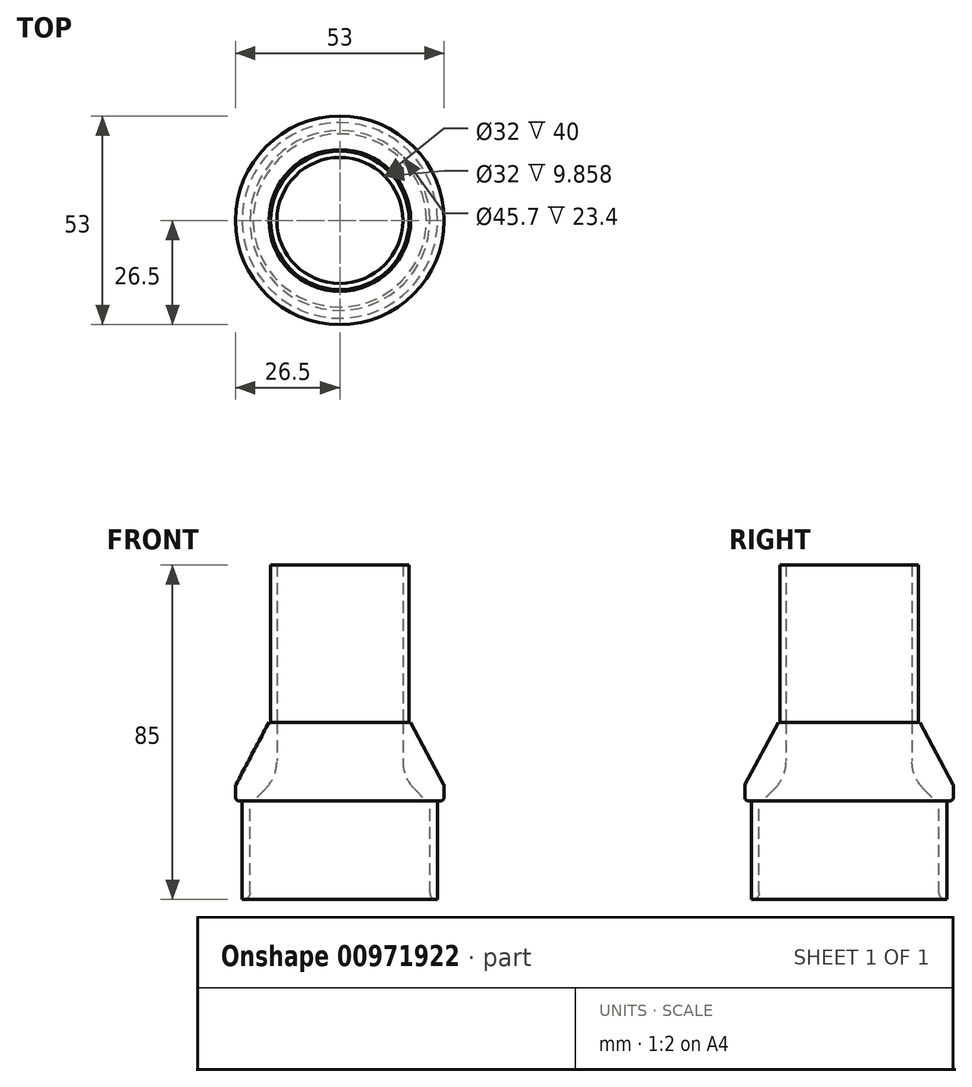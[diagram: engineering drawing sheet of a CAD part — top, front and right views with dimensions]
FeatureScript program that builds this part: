
annotation { "Feature Type Name" : "Feature", "Feature Type Description" : "" }
export const myFeature = defineFeature(function(context is Context, id is Id, definition is map)
    precondition{}
    {
        {
            var Q0;
            Q0=qCreatedBy(makeId("Top.planeOp"),FACE);
            var sketch = newSketch(context, id + "F0", { "sketchPlane" : qUnion([Q0])});
            skCircle(sketch, "E0", {"center": v(0, 0) * mm, "radius": 24.85 * mm});
            skCircle(sketch, "E1", {"center": v(0, 0) * mm, "radius": 22.85 * mm});
            skCircle(sketch, "E2", {"center": v(0, 0) * mm, "radius": 26.5 * mm});
            skCircle(sketch, "E3", {"center": v(0, 0) * mm, "radius": 17.6 * mm});
            skCircle(sketch, "E4", {"center": v(0, 0) * mm, "radius": 16 * mm});
            skSolve(sketch);
        }
        {
            var Q0;
            Q0=makeQuery(id+"F0.imprint","IMPRINT",FACE,{"disambiguationData":[TD([[makeQuery(id+"F0.imprint","IMPRINT",EDGE,{"derivedFrom":sQuery(id+"F0.wireOp",EDGE,"E0")}),1.0]])]});
            extrude(context, id + "F1", {"entities" : qUnion([Q0]), "oppositeDirection" : true, "depth" : 25 * mm, "offsetDistance" : 25 * mm});
        }
        {
            var Q0;
            Q0=makeQuery(id+"F0.imprint","IMPRINT",FACE,{"disambiguationData":[TD([[makeQuery(id+"F0.imprint","IMPRINT",EDGE,{"derivedFrom":sQuery(id+"F0.wireOp",EDGE,"E3")}),1.0]])]});
            extrude(context, id + "F2", {"entities" : qUnion([Q0]), "depth" : 60 * mm, "offsetDistance" : 25 * mm, "hasSecondDirection" : true, "secondDirectionOppositeDirection" : false, "secondDirectionDepth" : 20 * mm});
        }
        {
            var Q0;
            Q0=makeQuery(id+"F0.imprint","IMPRINT",FACE,{"disambiguationData":[TD([[makeQuery(id+"F0.imprint","IMPRINT",EDGE,{"derivedFrom":sQuery(id+"F0.wireOp",EDGE,"E3")}),1.0]])]});
            var Q1;
            Q1=makeQuery(id+"F0.imprint","IMPRINT",FACE,{"disambiguationData":[TD([[makeQuery(id+"F0.imprint","IMPRINT",EDGE,{"derivedFrom":sQuery(id+"F0.wireOp",EDGE,"E1")}),1.0]])]});
            var Q2;
            Q2=makeQuery(id+"F0.imprint","IMPRINT",FACE,{"disambiguationData":[TD([[makeQuery(id+"F0.imprint","IMPRINT",EDGE,{"derivedFrom":sQuery(id+"F0.wireOp",EDGE,"E0")}),1.0]])]});
            var Q3;
            Q3=makeQuery(id+"F0.imprint","IMPRINT",FACE,{"disambiguationData":[TD([[makeQuery(id+"F0.imprint","IMPRINT",EDGE,{"derivedFrom":sQuery(id+"F0.wireOp",EDGE,"E0")}),-1.0]])]});
            extrude(context, id + "F3", {"entities" : qUnion([Q0, Q1, Q2, Q3]), "depth" : 20 * mm, "offsetDistance" : 25 * mm});
        }
        {
            var Q0;
            Q0=makeQuery(id+"F3.opExtrude","CAP_EDGE",EDGE,{"disambiguationData":[OSD([sQuery(id+"F0.wireOp",EDGE,"E2")])],"isStart":false});
            chamfer(context, id + "F4", {"entities" : qUnion([Q0]), "chamferType" : ChamferType.TWO_OFFSETS, "width1" : 8.5 * mm, "oppositeDirection" : false, "width2" : 16 * mm, "tangentPropagation" : true});
        }
        {
            var Q0;
            Q0=makeQuery(id+"F3.opExtrude","CAP_EDGE",EDGE,{"disambiguationData":[OSD([sQuery(id+"F0.wireOp",EDGE,"E4")])],"isStart":true});
            chamfer(context, id + "F5", {"entities" : qUnion([Q0]), "width" : 6 * mm, "tangentPropagation" : true});
        }
        {
            var Q0;
            {var subQ0=sQuery(id+"F0.wireOp",EDGE,"E4");Q0=makeQuery(id+"F5.opChamfer","BLEND_EDGE",EDGE,{"blendedFrom":[makeQuery(id+"F3.opExtrude","CAP_EDGE",EDGE,{"disambiguationData":[OSD([subQ0])],"isStart":true}),makeQuery(id+"F3.opExtrude","SWEPT_FACE",FACE,{"disambiguationData":[OSD([subQ0])]})],"blendedInto":[makeQuery(id+"F3.opExtrude","SWEPT_FACE",FACE,{"disambiguationData":[OSD([subQ0])]})]});}
            fillet(context, id + "F6", {"entities" : qUnion([Q0]), "tangentPropagation" : true, "radius" : 10 * mm, "defaultsChanged" : true, "vertexSettings" : [], "allowEdgeOverflow" : false});
        }
        {
            var Q0;
            Q0=makeQuery(id+"F1.opExtrude","CAP_EDGE",EDGE,{"disambiguationData":[OSD([sQuery(id+"F0.wireOp",EDGE,"E1")])],"isStart":false});
            fillet(context, id + "F7", {"entities" : qUnion([Q0]), "tangentPropagation" : true, "radius" : 1.6 * mm, "defaultsChanged" : true, "vertexSettings" : [], "allowEdgeOverflow" : false});
        }
        {
            var Q0;
            Q0=makeQuery(id+"F3.opExtrude","CAP_EDGE",EDGE,{"disambiguationData":[OSD([sQuery(id+"F0.wireOp",EDGE,"E2")])],"isStart":true});
            var Q1;
            {var subQ0=sQuery(id+"F0.wireOp",EDGE,"E2");Q1=makeQuery(id+"F4.opChamfer","BLEND_EDGE",EDGE,{"blendedFrom":[makeQuery(id+"F3.opExtrude","CAP_EDGE",EDGE,{"disambiguationData":[OSD([subQ0])],"isStart":false}),makeQuery(id+"F3.opExtrude","SWEPT_FACE",FACE,{"disambiguationData":[OSD([subQ0])]})],"blendedInto":[makeQuery(id+"F3.opExtrude","SWEPT_FACE",FACE,{"disambiguationData":[OSD([subQ0])]})]});}
            fillet(context, id + "F8", {"entities" : qUnion([Q0, Q1]), "tangentPropagation" : true, "radius" : 1 * mm, "defaultsChanged" : false, "vertexSettings" : [], "allowEdgeOverflow" : false});
        }
    });
